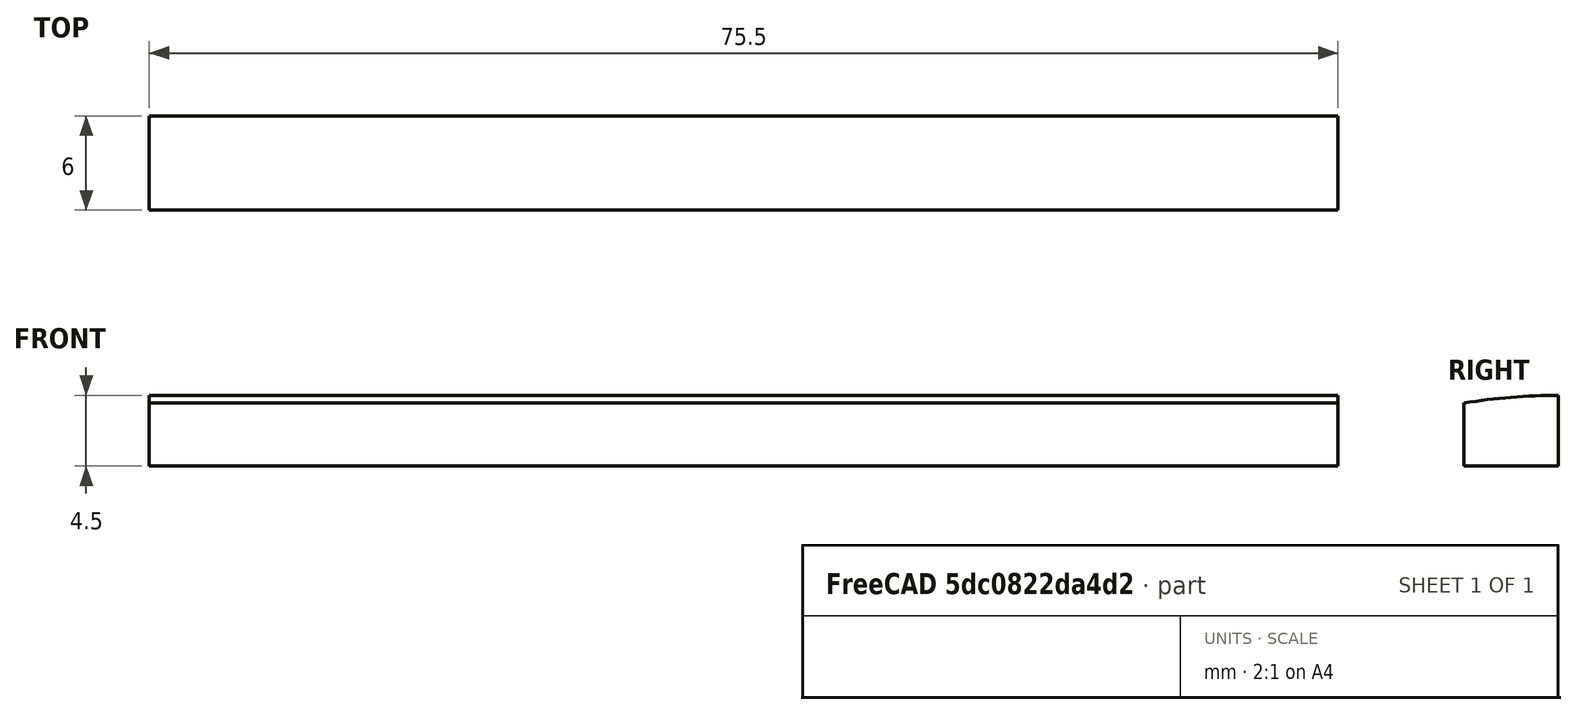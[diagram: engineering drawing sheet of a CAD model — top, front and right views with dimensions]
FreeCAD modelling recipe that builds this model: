
FCSTD DOCUMENT  (FreeCAD 1.0R39109 (Git))
Label: touchpad blank
License: All rights reserved
LicenseURL: http://en.wikipedia.org/wiki/All_rights_reserved
objects: Sketcher::SketchObject×1, PartDesign::Pad×1, PartDesign::Body×1
note: 6 computed .brp shape members not serialized (recipe doc carries the construction recipe); baked Part::Feature solids carry a one-line shape summary decoded from their .brp

FEATURE [Sketcher::SketchObject] Sketch
  ArcFitTolerance = 1e-06
  AttachmentSupport = -> [YZ_Plane]
  FullyConstrained = true
  MakeInternals = false
  MapMode = 5
  Placement = pos=(0,0,0) rot=(0.57735,0.57735,0.57735;2.0944rad)
  sketch-geometry (4):
    g0: LineSegment StartX=-3 StartY=-2.25 StartZ=0 EndX=3 EndY=-2.25 EndZ=0
    g1: LineSegment StartX=3 StartY=-2.25 StartZ=0 EndX=3 EndY=2.25 EndZ=0
    g2: LineSegment StartX=-3 StartY=-2.25 StartZ=0 EndX=-3 EndY=1.75 EndZ=0
    g3: ArcOfCircle CenterX=3 CenterY=-34 CenterZ=0 NormalX=0 NormalY=0 NormalZ=1 AngleXU=0 Radius=36.25 StartAngle=1.5708 EndAngle=1.73708
  constraints (12):
    c: Horizontal(g0)
    c: DistanceX(g0,g0) = 6
    c: DistanceX(g-1,g0) = 3
    c: Distance(g1) = 4.5
    c: Vertical(g1)
    c: Coincident(g0,g1)
    c: DistanceY(g-1,g1) = 2.25
    c: Distance(g2) = 4
    c: Coincident(g2,g0)
    c: Vertical(g2)
    c: Perpendicular(g1,g3) = 1.5708
    c: Coincident(g3,g2)
FEATURE [PartDesign::Pad] Pad
  Direction = (1,0,0)
  Length = 75.5
  Length2 = 10
  Placement = pos=(0,0,0) rot=(1,1,1;2.0944rad)
  Profile = -> Sketch
  ReferenceAxis = -> Sketch [N_Axis]
  Suppressed = false
  Type = 0
FEATURE [PartDesign::Body] Body
  AllowCompound = false
  Group = -> [Sketch,Pad]
  Origin = -> Origin
  Tip = -> Pad
